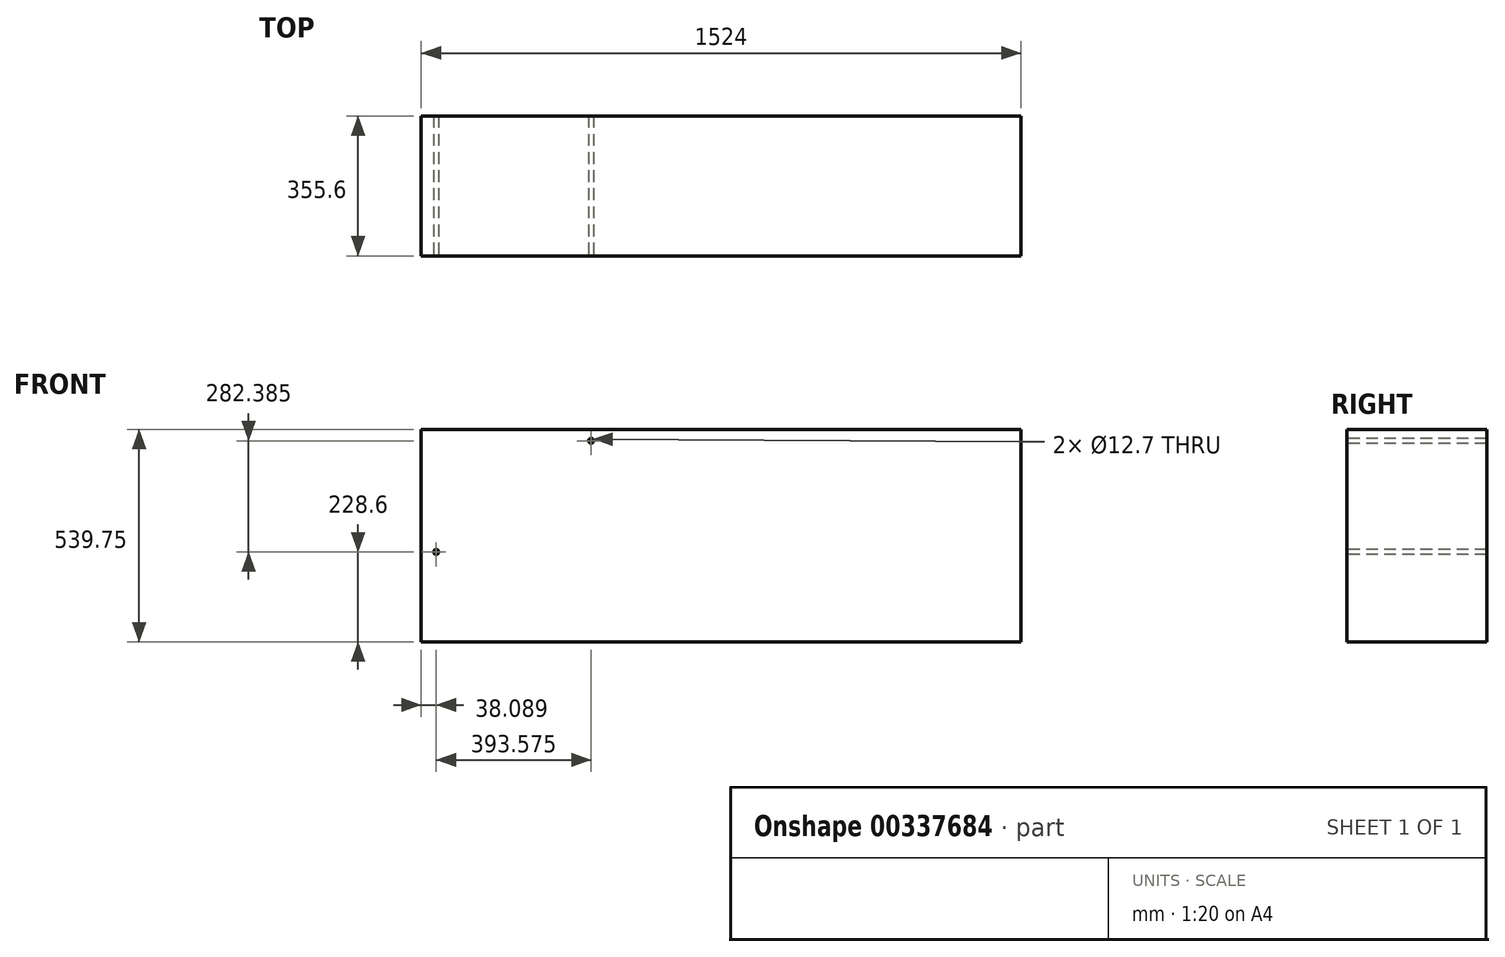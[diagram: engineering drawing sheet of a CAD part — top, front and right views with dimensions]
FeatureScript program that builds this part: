
annotation { "Feature Type Name" : "Feature", "Feature Type Description" : "" }
export const myFeature = defineFeature(function(context is Context, id is Id, definition is map)
    precondition{}
    {
        {
            var Q0;
            Q0=qCreatedBy(makeId("Top.planeOp"),FACE);
            var sketch = newSketch(context, id + "F0", { "sketchPlane" : qUnion([Q0])});
            skLineSegment(sketch, "E0.bottom", {"start": v(12.97, 0) * mm, "end": v(1536.97, 0) * mm});
            skLineSegment(sketch, "E0.top", {"start": v(12.97, 355.6) * mm, "end": v(1536.97, 355.6) * mm});
            skLineSegment(sketch, "E0.left", {"start": v(12.97, 0) * mm, "end": v(12.97, 355.6) * mm});
            skLineSegment(sketch, "E0.right", {"start": v(1536.97, 0) * mm, "end": v(1536.97, 355.6) * mm});
            skSolve(sketch);
        }
        {
            var Q0;
            Q0=makeQuery(id+"F0.imprint","IMPRINT",FACE,{"disambiguationData":[TD([[makeQuery(id+"F0.imprint","IMPRINT",EDGE,{"derivedFrom":sQuery(id+"F0.wireOp",EDGE,"E0.bottom")}),1.0]])]});
            extrude(context, id + "F1", {"entities" : qUnion([Q0]), "depth" : 539.75 * mm});
        }
        {
            var Q0;
            Q0=makeQuery(id+"F1.opExtrude","SWEPT_FACE",FACE,{"disambiguationData":[OSD([sQuery(id+"F0.wireOp",EDGE,"E0.bottom")])]});
            var sketch = newSketch(context, id + "F2", { "sketchPlane" : qUnion([Q0])});
            skCircle(sketch, "E1", {"center": v(51.06, 228.6) * mm, "radius": 6.35 * mm});
            skCircle(sketch, "E2", {"center": v(444.63, 510.99) * mm, "radius": 6.35 * mm});
            skSolve(sketch);
        }
        {
            var Q0;
            Q0=sQuery(id+"F2.wireOp",VERTEX,"E2.center");
            var Q1;
            Q1=sQuery(id+"F2.wireOp",VERTEX,"E1.center");
            var Q2;
            Q2=makeQuery(id+"F1.opExtrude","SWEPT_BODY",BODY,{"disambiguationData":[OSD([sQuery(id+"F0.wireOp",EDGE,"E0.bottom"),sQuery(id+"F0.wireOp",EDGE,"E0.top"),sQuery(id+"F0.wireOp",EDGE,"E0.left"),sQuery(id+"F0.wireOp",EDGE,"E0.right")])]});
            hole(context, id + "F3", {"style" : HoleStyle.SIMPLE, "endStyle" : HoleEndStyle.THROUGH, "holeDiameter" : 12.7 * mm, "isTappedThrough" : true, "tappedDepth" : 12.7 * mm, "tapClearance" : 3, "locations" : qUnion([Q0, Q1]), "scope" : qUnion([Q2])});
        }
    });
